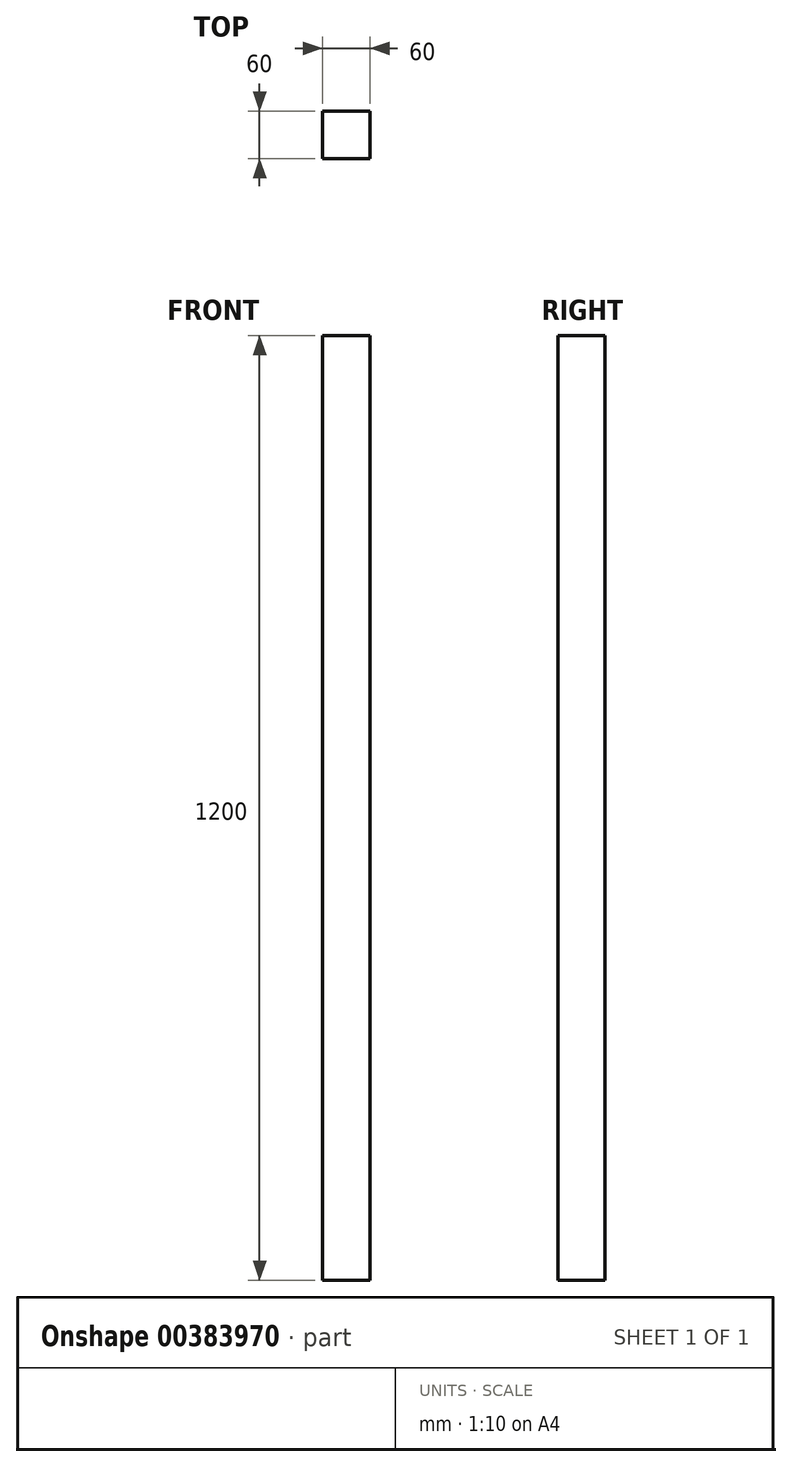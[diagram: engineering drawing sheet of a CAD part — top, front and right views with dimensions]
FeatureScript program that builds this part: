
annotation { "Feature Type Name" : "Feature", "Feature Type Description" : "" }
export const myFeature = defineFeature(function(context is Context, id is Id, definition is map)
    precondition{}
    {
        {
            var Q0;
            Q0=qCreatedBy(makeId("Front.planeOp"),FACE);
            var sketch = newSketch(context, id + "F0", { "sketchPlane" : qUnion([Q0])});
            skLineSegment(sketch, "E0.bottom", {"start": v(30, 600) * mm, "end": v(-30, 600) * mm});
            skLineSegment(sketch, "E0.top", {"start": v(30, -600) * mm, "end": v(-30, -600) * mm});
            skLineSegment(sketch, "E0.left", {"start": v(30, 600) * mm, "end": v(30, -600) * mm});
            skLineSegment(sketch, "E0.right", {"start": v(-30, 600) * mm, "end": v(-30, -600) * mm});
            skPoint(sketch, "E0.middle", {"position": v(0, 0) * mm});
            skSolve(sketch);
        }
        {
            var Q0;
            Q0=makeQuery(id+"F0.imprint","IMPRINT",FACE,{"disambiguationData":[TD([[makeQuery(id+"F0.imprint","IMPRINT",EDGE,{"derivedFrom":sQuery(id+"F0.wireOp",EDGE,"E0.bottom")}),1.0]])]});
            extrude(context, id + "F1", {"entities" : qUnion([Q0]), "endBound" : BoundingType.SYMMETRIC, "depth" : 60 * mm});
        }
    });
